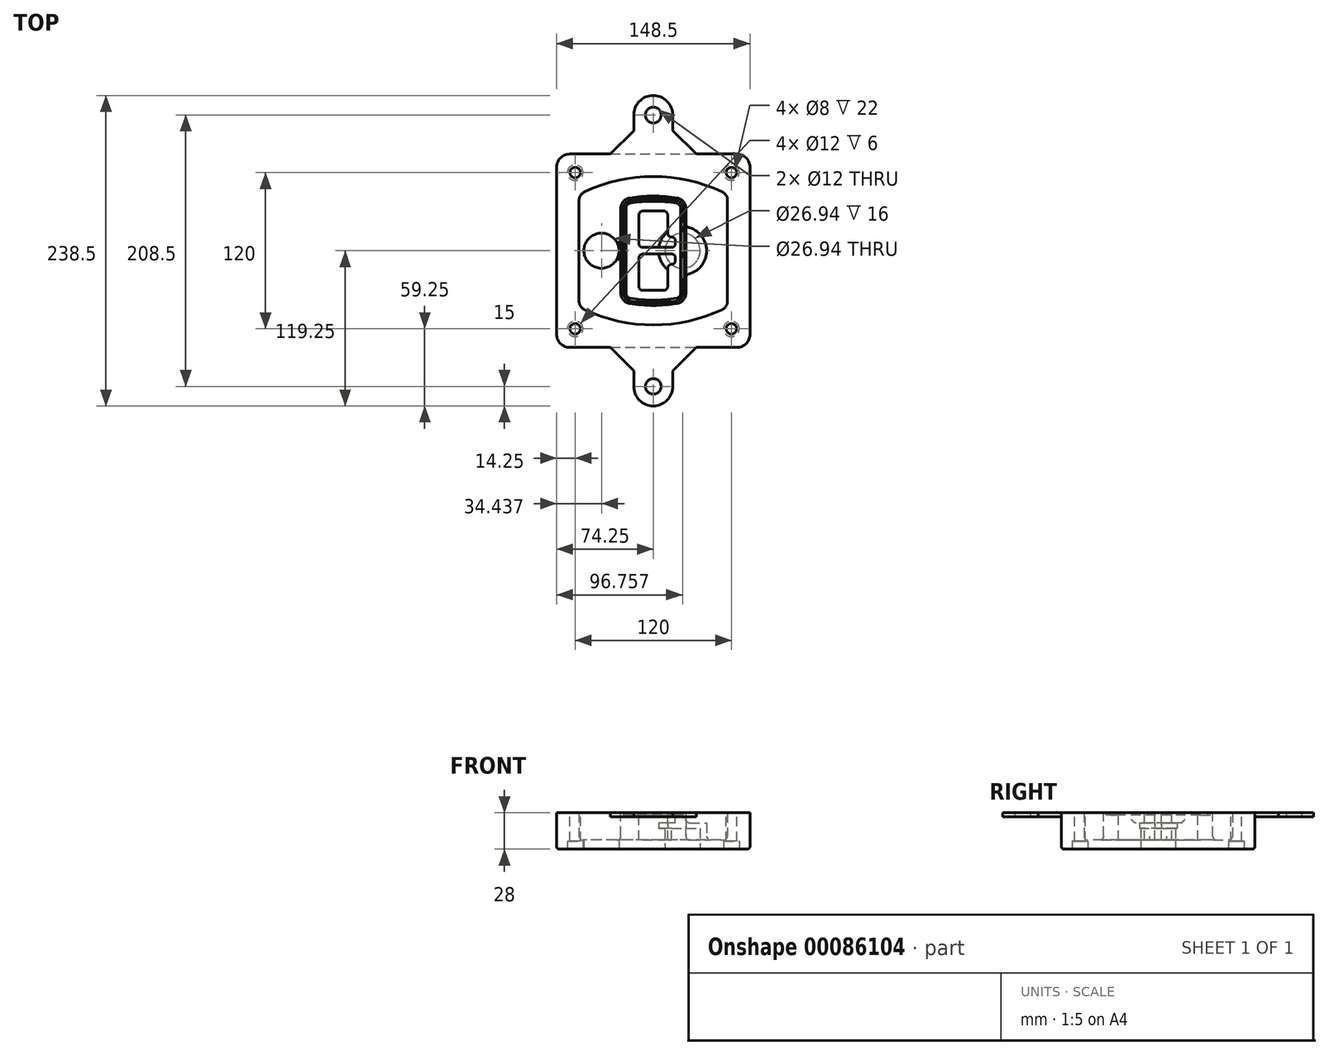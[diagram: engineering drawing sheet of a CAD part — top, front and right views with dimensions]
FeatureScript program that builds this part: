
annotation { "Feature Type Name" : "Feature", "Feature Type Description" : "" }
export const myFeature = defineFeature(function(context is Context, id is Id, definition is map)
    precondition{}
    {
        {
            var Q0;
            Q0=qCreatedBy(makeId("Top.planeOp"),FACE);
            var sketch = newSketch(context, id + "F0", { "sketchPlane" : qUnion([Q0])});
            skPoint(sketch, "E0.rect.middle", {"position": v(0, 0) * mm});
            skLineSegment(sketch, "E1.bottom", {"start": v(-64.25, -74.25) * mm, "end": v(64.25, -74.25) * mm});
            skLineSegment(sketch, "E1.top", {"start": v(-64.25, 74.25) * mm, "end": v(64.25, 74.25) * mm});
            skLineSegment(sketch, "E1.left", {"start": v(-74.25, -64.25) * mm, "end": v(-74.25, 64.25) * mm});
            skLineSegment(sketch, "E1.right", {"start": v(74.25, -64.25) * mm, "end": v(74.25, 64.25) * mm});
            skLineSegment(sketch, "E2", {"start": v(-74.25, 74.25) * mm, "end": v(74.25, -74.25) * mm, "construction": true});
            skLineSegment(sketch, "E3", {"start": v(74.25, 74.25) * mm, "end": v(-74.25, -74.25) * mm, "construction": true});
            skCircle(sketch, "E4", {"center": v(-60, 60) * mm, "radius": 4 * mm});
            skCircle(sketch, "E5", {"center": v(60, 60) * mm, "radius": 4 * mm});
            skCircle(sketch, "E6", {"center": v(60, -60) * mm, "radius": 4 * mm});
            skCircle(sketch, "E7", {"center": v(-60, -60) * mm, "radius": 4 * mm});
            skLineSegment(sketch, "E8", {"start": v(-60, 60) * mm, "end": v(60, 60) * mm, "construction": true});
            skLineSegment(sketch, "E9", {"start": v(60, 60) * mm, "end": v(60, -60) * mm, "construction": true});
            skLineSegment(sketch, "E10", {"start": v(60, -60) * mm, "end": v(-60, -60) * mm, "construction": true});
            skLineSegment(sketch, "E11", {"start": v(-60, -60) * mm, "end": v(-60, 60) * mm, "construction": true});
            skLineSegment(sketch, "E12", {"start": v(-60, 38.83) * mm, "end": v(-60, -38.83) * mm});
            skLineSegment(sketch, "E13", {"start": v(60, 38.83) * mm, "end": v(60, -38.83) * mm});
            skArc(sketch, "E14", {"start": v(54.26, 47.88) * mm, "mid": v(0, 60) * mm, "end": v(-54.26, 47.88) * mm});
            skArc(sketch, "E15", {"start": v(-54.26, -47.88) * mm, "mid": v(0, -60) * mm, "end": v(54.26, -47.88) * mm});
            skLineSegment(sketch, "E16", {"start": v(-60, 0) * mm, "end": v(60, 0) * mm, "construction": true});
            skPoint(sketch, "E17.visualSharp", {"position": v(-60, -45) * mm});
            skArc(sketch, "E17.filletArc", {"start": v(-60, -38.83) * mm, "mid": v(-58.44, -44.2) * mm, "end": v(-54.26, -47.88) * mm});
            skPoint(sketch, "E18.visualSharp", {"position": v(-60, 45) * mm});
            skArc(sketch, "E18.filletArc", {"start": v(-54.26, 47.88) * mm, "mid": v(-58.44, 44.2) * mm, "end": v(-60, 38.83) * mm});
            skPoint(sketch, "E19.visualSharp", {"position": v(60, 45) * mm});
            skArc(sketch, "E19.filletArc", {"start": v(60, 38.83) * mm, "mid": v(58.44, 44.2) * mm, "end": v(54.26, 47.88) * mm});
            skPoint(sketch, "E20.visualSharp", {"position": v(60, -45) * mm});
            skArc(sketch, "E20.filletArc", {"start": v(54.26, -47.88) * mm, "mid": v(58.44, -44.2) * mm, "end": v(60, -38.83) * mm});
            skPoint(sketch, "E21.visualSharp", {"position": v(-74.25, 74.25) * mm});
            skArc(sketch, "E21.filletArc", {"start": v(-64.25, 74.25) * mm, "mid": v(-71.32, 71.32) * mm, "end": v(-74.25, 64.25) * mm});
            skPoint(sketch, "E22.visualSharp", {"position": v(74.25, 74.25) * mm});
            skArc(sketch, "E22.filletArc", {"start": v(74.25, 64.25) * mm, "mid": v(71.32, 71.32) * mm, "end": v(64.25, 74.25) * mm});
            skPoint(sketch, "E23.visualSharp", {"position": v(74.25, -74.25) * mm});
            skArc(sketch, "E23.filletArc", {"start": v(64.25, -74.25) * mm, "mid": v(71.32, -71.32) * mm, "end": v(74.25, -64.25) * mm});
            skPoint(sketch, "E24.visualSharp", {"position": v(-74.25, -74.25) * mm});
            skArc(sketch, "E24.filletArc", {"start": v(-74.25, -64.25) * mm, "mid": v(-71.32, -71.32) * mm, "end": v(-64.25, -74.25) * mm});
            skArc(sketch, "E25.0", {"start": v(57, 38.83) * mm, "mid": v(55.9, 42.58) * mm, "end": v(52.98, 45.17) * mm});
            skLineSegment(sketch, "E25.1", {"start": v(57, 38.83) * mm, "end": v(57, -38.83) * mm});
            skArc(sketch, "E25.2", {"start": v(52.98, -45.17) * mm, "mid": v(55.9, -42.58) * mm, "end": v(57, -38.83) * mm});
            skArc(sketch, "E25.3", {"start": v(-52.98, -45.17) * mm, "mid": v(0, -57) * mm, "end": v(52.98, -45.17) * mm});
            skArc(sketch, "E25.4", {"start": v(-57, -38.83) * mm, "mid": v(-55.9, -42.58) * mm, "end": v(-52.98, -45.17) * mm});
            skArc(sketch, "E25.5", {"start": v(52.98, 45.17) * mm, "mid": v(0, 57) * mm, "end": v(-52.98, 45.17) * mm});
            skLineSegment(sketch, "E25.6", {"start": v(-57, 38.83) * mm, "end": v(-57, -38.83) * mm});
            skArc(sketch, "E25.7", {"start": v(-52.98, 45.17) * mm, "mid": v(-55.9, 42.58) * mm, "end": v(-57, 38.83) * mm});
            skArc(sketch, "E26.0", {"start": v(-55.96, 51.5) * mm, "mid": v(-61.82, 46.33) * mm, "end": v(-64, 38.83) * mm});
            skArc(sketch, "E26.1", {"start": v(55.96, 51.5) * mm, "mid": v(0, 64) * mm, "end": v(-55.96, 51.5) * mm});
            skArc(sketch, "E26.2", {"start": v(64, 38.83) * mm, "mid": v(61.82, 46.33) * mm, "end": v(55.96, 51.5) * mm});
            skLineSegment(sketch, "E26.3", {"start": v(64, 38.83) * mm, "end": v(64, -38.83) * mm});
            skArc(sketch, "E26.4", {"start": v(55.96, -51.5) * mm, "mid": v(61.82, -46.33) * mm, "end": v(64, -38.83) * mm});
            skLineSegment(sketch, "E26.5", {"start": v(-64, 38.83) * mm, "end": v(-64, -38.83) * mm});
            skArc(sketch, "E26.6", {"start": v(-55.96, -51.5) * mm, "mid": v(0, -64) * mm, "end": v(55.96, -51.5) * mm});
            skArc(sketch, "E26.7", {"start": v(-64, -38.83) * mm, "mid": v(-61.82, -46.33) * mm, "end": v(-55.96, -51.5) * mm});
            skSolve(sketch);
        }
        {
            var Q0;
            Q0=makeQuery(id+"F0.imprint","IMPRINT",FACE,{"disambiguationData":[TD([[makeQuery(id+"F0.imprint","IMPRINT",EDGE,{"derivedFrom":sQuery(id+"F0.wireOp",EDGE,"E1.bottom")}),1.0]])]});
            var Q1;
            Q1=makeQuery(id+"F0.imprint","IMPRINT",FACE,{"disambiguationData":[TD([[makeQuery(id+"F0.imprint","IMPRINT",EDGE,{"derivedFrom":sQuery(id+"F0.wireOp",EDGE,"E12")}),1.0]])]});
            var Q2;
            Q2=makeQuery(id+"F0.imprint","IMPRINT",FACE,{"disambiguationData":[TD([[makeQuery(id+"F0.imprint","IMPRINT",EDGE,{"derivedFrom":sQuery(id+"F0.wireOp",EDGE,"E25.0")}),1.0]])]});
            var Q3;
            Q3=makeQuery(id+"F0.imprint","IMPRINT",FACE,{"disambiguationData":[TD([[makeQuery(id+"F0.imprint","IMPRINT",EDGE,{"derivedFrom":sQuery(id+"F0.wireOp",EDGE,"E12")}),-1.0]])]});
            extrude(context, id + "F1", {"entities" : qUnion([Q0, Q1, Q2, Q3]), "oppositeDirection" : true, "depth" : 25 * mm});
        }
        {
            var Q0;
            Q0=makeQuery(id+"F0.imprint","IMPRINT",FACE,{"disambiguationData":[TD([[makeQuery(id+"F0.imprint","IMPRINT",EDGE,{"derivedFrom":sQuery(id+"F0.wireOp",EDGE,"E12")}),1.0]])]});
            extrude(context, id + "F2", {"entities" : qUnion([Q0]), "operationType" : NewBodyOperationType.ADD, "depth" : 3 * mm});
        }
        {
            var Q0;
            Q0=makeQuery(id+"F0.imprint","IMPRINT",FACE,{"disambiguationData":[TD([[makeQuery(id+"F0.imprint","IMPRINT",EDGE,{"derivedFrom":sQuery(id+"F0.wireOp",EDGE,"E25.0")}),1.0]])]});
            extrude(context, id + "F3", {"entities" : qUnion([Q0]), "operationType" : NewBodyOperationType.REMOVE, "oppositeDirection" : true, "depth" : 18 * mm});
        }
        {
            var Q0;
            Q0=makeQuery(id+"F2.opExtrude","CAP_FACE",FACE,{"disambiguationData":[OSD([sQuery(id+"F0.wireOp",EDGE,"E12"),sQuery(id+"F0.wireOp",EDGE,"E13"),sQuery(id+"F0.wireOp",EDGE,"E14"),sQuery(id+"F0.wireOp",EDGE,"E15"),sQuery(id+"F0.wireOp",EDGE,"E17.filletArc"),sQuery(id+"F0.wireOp",EDGE,"E18.filletArc"),sQuery(id+"F0.wireOp",EDGE,"E19.filletArc"),sQuery(id+"F0.wireOp",EDGE,"E20.filletArc"),sQuery(id+"F0.wireOp",EDGE,"E25.0"),sQuery(id+"F0.wireOp",EDGE,"E25.1"),sQuery(id+"F0.wireOp",EDGE,"E25.2"),sQuery(id+"F0.wireOp",EDGE,"E25.3"),sQuery(id+"F0.wireOp",EDGE,"E25.4"),sQuery(id+"F0.wireOp",EDGE,"E25.5"),sQuery(id+"F0.wireOp",EDGE,"E25.6"),sQuery(id+"F0.wireOp",EDGE,"E25.7")])],"isStart":false});
            var sketch = newSketch(context, id + "F4", { "sketchPlane" : qUnion([Q0])});
            skArc(sketch, "E27.0", {"start": v(-18.34, -40.45) * mm, "mid": v(0, -42) * mm, "end": v(18.34, -40.45) * mm});
            skArc(sketch, "E28.0", {"start": v(18.34, 40.45) * mm, "mid": v(0, 42) * mm, "end": v(-18.34, 40.45) * mm});
            skLineSegment(sketch, "E29", {"start": v(-25, 32.57) * mm, "end": v(-25, -32.57) * mm});
            skLineSegment(sketch, "E30", {"start": v(25, 32.57) * mm, "end": v(25, -32.57) * mm});
            skLineSegment(sketch, "E31", {"start": v(-25, 39.1) * mm, "end": v(25, 39.1) * mm, "construction": true});
            skLineSegment(sketch, "E32", {"start": v(-25, -39.1) * mm, "end": v(25, -39.1) * mm, "construction": true});
            skPoint(sketch, "E33.visualSharp", {"position": v(-25, 39.1) * mm});
            skArc(sketch, "E33.filletArc", {"start": v(-18.34, 40.45) * mm, "mid": v(-23.11, 37.73) * mm, "end": v(-25, 32.57) * mm});
            skPoint(sketch, "E34.visualSharp", {"position": v(25, 39.1) * mm});
            skArc(sketch, "E34.filletArc", {"start": v(25, 32.57) * mm, "mid": v(23.11, 37.73) * mm, "end": v(18.34, 40.45) * mm});
            skPoint(sketch, "E35.visualSharp", {"position": v(25, -39.1) * mm});
            skArc(sketch, "E35.filletArc", {"start": v(18.34, -40.45) * mm, "mid": v(23.11, -37.73) * mm, "end": v(25, -32.57) * mm});
            skPoint(sketch, "E36.visualSharp", {"position": v(-25, -39.1) * mm});
            skArc(sketch, "E36.filletArc", {"start": v(-25, -32.57) * mm, "mid": v(-23.11, -37.73) * mm, "end": v(-18.34, -40.45) * mm});
            skArc(sketch, "E37.0", {"start": v(52.98, 45.17) * mm, "mid": v(0, 57) * mm, "end": v(-52.98, 45.17) * mm});
            skArc(sketch, "E37.1", {"start": v(-52.98, 45.17) * mm, "mid": v(-55.9, 42.58) * mm, "end": v(-57, 38.83) * mm});
            skLineSegment(sketch, "E37.2", {"start": v(-57, 38.83) * mm, "end": v(-57, -38.83) * mm});
            skArc(sketch, "E37.3", {"start": v(-57, -38.83) * mm, "mid": v(-55.9, -42.58) * mm, "end": v(-52.98, -45.17) * mm});
            skArc(sketch, "E37.4", {"start": v(-52.98, -45.17) * mm, "mid": v(0, -57) * mm, "end": v(52.98, -45.17) * mm});
            skArc(sketch, "E37.5", {"start": v(52.98, -45.17) * mm, "mid": v(55.9, -42.58) * mm, "end": v(57, -38.83) * mm});
            skLineSegment(sketch, "E37.6", {"start": v(57, 38.83) * mm, "end": v(57, -38.83) * mm});
            skArc(sketch, "E37.7", {"start": v(57, 38.83) * mm, "mid": v(55.9, 42.58) * mm, "end": v(52.98, 45.17) * mm});
            skLineSegment(sketch, "E38.0", {"start": v(23, 32.57) * mm, "end": v(23, -32.57) * mm});
            skArc(sketch, "E38.1", {"start": v(18, -38.48) * mm, "mid": v(21.58, -36.44) * mm, "end": v(23, -32.57) * mm});
            skArc(sketch, "E38.2", {"start": v(-18, -38.48) * mm, "mid": v(0, -40) * mm, "end": v(18, -38.48) * mm});
            skArc(sketch, "E38.3", {"start": v(-23, -32.57) * mm, "mid": v(-21.58, -36.44) * mm, "end": v(-18, -38.48) * mm});
            skLineSegment(sketch, "E38.4", {"start": v(-23, 32.57) * mm, "end": v(-23, -32.57) * mm});
            skArc(sketch, "E38.5", {"start": v(23, 32.57) * mm, "mid": v(21.58, 36.44) * mm, "end": v(18, 38.48) * mm});
            skArc(sketch, "E38.6", {"start": v(-18, 38.48) * mm, "mid": v(-21.58, 36.44) * mm, "end": v(-23, 32.57) * mm});
            skArc(sketch, "E38.7", {"start": v(18, 38.48) * mm, "mid": v(0, 40) * mm, "end": v(-18, 38.48) * mm});
            skArc(sketch, "E39.0", {"start": v(21, 32.57) * mm, "mid": v(20.06, 35.15) * mm, "end": v(17.67, 36.5) * mm});
            skLineSegment(sketch, "E39.1", {"start": v(21, 32.57) * mm, "end": v(21, -32.57) * mm});
            skArc(sketch, "E39.2", {"start": v(17.67, -36.5) * mm, "mid": v(20.06, -35.15) * mm, "end": v(21, -32.57) * mm});
            skArc(sketch, "E39.3", {"start": v(-17.67, -36.5) * mm, "mid": v(0, -38) * mm, "end": v(17.67, -36.5) * mm});
            skArc(sketch, "E39.4", {"start": v(-21, -32.57) * mm, "mid": v(-20.06, -35.15) * mm, "end": v(-17.67, -36.5) * mm});
            skArc(sketch, "E39.5", {"start": v(17.67, 36.5) * mm, "mid": v(0, 38) * mm, "end": v(-17.67, 36.5) * mm});
            skLineSegment(sketch, "E39.6", {"start": v(-21, 32.57) * mm, "end": v(-21, -32.57) * mm});
            skArc(sketch, "E39.7", {"start": v(-17.67, 36.5) * mm, "mid": v(-20.06, 35.15) * mm, "end": v(-21, 32.57) * mm});
            skLineSegment(sketch, "E40", {"start": v(-25, 0) * mm, "end": v(25, 0) * mm, "construction": true});
            skLineSegment(sketch, "E41", {"start": v(-11, 5.5) * mm, "end": v(-11, 27.5) * mm});
            skLineSegment(sketch, "E42", {"start": v(-8, 30.5) * mm, "end": v(8, 30.5) * mm});
            skLineSegment(sketch, "E43", {"start": v(11, 27.5) * mm, "end": v(11, 13.5) * mm});
            skLineSegment(sketch, "E44", {"start": v(14, 10.5) * mm, "end": v(14, 10.5) * mm});
            skLineSegment(sketch, "E45", {"start": v(17, 7.5) * mm, "end": v(17, 5.5) * mm});
            skLineSegment(sketch, "E46", {"start": v(14, 2.5) * mm, "end": v(-8, 2.5) * mm});
            skPoint(sketch, "E47.visualSharp", {"position": v(-11, 30.5) * mm});
            skArc(sketch, "E47.filletArc", {"start": v(-8, 30.5) * mm, "mid": v(-10.12, 29.62) * mm, "end": v(-11, 27.5) * mm});
            skPoint(sketch, "E48.visualSharp", {"position": v(11, 30.5) * mm});
            skArc(sketch, "E48.filletArc", {"start": v(11, 27.5) * mm, "mid": v(10.12, 29.62) * mm, "end": v(8, 30.5) * mm});
            skPoint(sketch, "E49.visualSharp", {"position": v(11, 10.5) * mm});
            skArc(sketch, "E49.filletArc", {"start": v(11, 13.5) * mm, "mid": v(11.88, 11.38) * mm, "end": v(14, 10.5) * mm});
            skPoint(sketch, "E50.visualSharp", {"position": v(17, 10.5) * mm});
            skArc(sketch, "E50.filletArc", {"start": v(17, 7.5) * mm, "mid": v(16.12, 9.62) * mm, "end": v(14, 10.5) * mm});
            skPoint(sketch, "E51.visualSharp", {"position": v(17, 2.5) * mm});
            skArc(sketch, "E51.filletArc", {"start": v(14, 2.5) * mm, "mid": v(16.12, 3.38) * mm, "end": v(17, 5.5) * mm});
            skPoint(sketch, "E52.visualSharp", {"position": v(-11, 2.5) * mm});
            skArc(sketch, "E52.filletArc", {"start": v(-11, 5.5) * mm, "mid": v(-10.12, 3.38) * mm, "end": v(-8, 2.5) * mm});
            skLineSegment(sketch, "E53.0.MirrorCS", {"start": v(14, -2.5) * mm, "end": v(-8, -2.5) * mm});
            skArc(sketch, "E54.0.MirrorCS", {"start": v(-11, -5.5) * mm, "mid": v(-10.12, -3.38) * mm, "end": v(-8, -2.5) * mm});
            skLineSegment(sketch, "E55.0.MirrorCS", {"start": v(-11, -5.5) * mm, "end": v(-11, -27.5) * mm});
            skArc(sketch, "E56.0.MirrorCS", {"start": v(-8, -30.5) * mm, "mid": v(-10.12, -29.62) * mm, "end": v(-11, -27.5) * mm});
            skLineSegment(sketch, "E57.0.MirrorCS", {"start": v(-8, -30.5) * mm, "end": v(8, -30.5) * mm});
            skArc(sketch, "E58.0.MirrorCS", {"start": v(11, -27.5) * mm, "mid": v(10.12, -29.62) * mm, "end": v(8, -30.5) * mm});
            skLineSegment(sketch, "E59.0.MirrorCS", {"start": v(11, -27.5) * mm, "end": v(11, -13.5) * mm});
            skArc(sketch, "E60.0.MirrorCS", {"start": v(11, -13.5) * mm, "mid": v(11.88, -11.38) * mm, "end": v(14, -10.5) * mm});
            skArc(sketch, "E61.0.MirrorCS", {"start": v(17, -7.5) * mm, "mid": v(16.12, -9.62) * mm, "end": v(14, -10.5) * mm});
            skLineSegment(sketch, "E62.0.MirrorCS", {"start": v(17, -7.5) * mm, "end": v(17, -5.5) * mm});
            skArc(sketch, "E63.0.MirrorCS", {"start": v(14, -2.5) * mm, "mid": v(16.12, -3.38) * mm, "end": v(17, -5.5) * mm});
            skSolve(sketch);
        }
        {
            var Q0;
            Q0=makeQuery(id+"F4.imprint","IMPRINT",FACE,{"disambiguationData":[TD([[makeQuery(id+"F4.imprint","IMPRINT",EDGE,{"derivedFrom":sQuery(id+"F4.wireOp",EDGE,"E27.0")}),1.0]])]});
            var Q1;
            Q1=makeQuery(id+"F4.imprint","IMPRINT",FACE,{"disambiguationData":[TD([[makeQuery(id+"F4.imprint","IMPRINT",EDGE,{"derivedFrom":sQuery(id+"F4.wireOp",EDGE,"E38.0")}),-1.0]])]});
            var Q2;
            Q2=makeQuery(id+"F4.imprint","IMPRINT",FACE,{"disambiguationData":[TD([[makeQuery(id+"F4.imprint","IMPRINT",EDGE,{"derivedFrom":sQuery(id+"F4.wireOp",EDGE,"E39.0")}),1.0]])]});
            extrude(context, id + "F5", {"entities" : qUnion([Q0, Q1, Q2]), "operationType" : NewBodyOperationType.ADD, "endBound" : BoundingType.UP_TO_NEXT, "oppositeDirection" : true, "depth" : 25 * mm});
        }
        {
            var Q0;
            Q0=makeQuery(id+"F4.imprint","IMPRINT",FACE,{"disambiguationData":[TD([[makeQuery(id+"F4.imprint","IMPRINT",EDGE,{"derivedFrom":sQuery(id+"F4.wireOp",EDGE,"E38.0")}),-1.0]])]});
            extrude(context, id + "F6", {"entities" : qUnion([Q0]), "operationType" : NewBodyOperationType.REMOVE, "oppositeDirection" : true, "depth" : 2 * mm});
        }
        {
            var Q0;
            Q0=makeQuery(id+"F1.opExtrude","CAP_FACE",FACE,{"disambiguationData":[OSD([sQuery(id+"F0.wireOp",EDGE,"E1.bottom"),sQuery(id+"F0.wireOp",EDGE,"E1.top"),sQuery(id+"F0.wireOp",EDGE,"E1.left"),sQuery(id+"F0.wireOp",EDGE,"E1.right"),sQuery(id+"F0.wireOp",EDGE,"E4"),sQuery(id+"F0.wireOp",EDGE,"E5"),sQuery(id+"F0.wireOp",EDGE,"E6"),sQuery(id+"F0.wireOp",EDGE,"E7"),sQuery(id+"F0.wireOp",EDGE,"E21.filletArc"),sQuery(id+"F0.wireOp",EDGE,"E22.filletArc"),sQuery(id+"F0.wireOp",EDGE,"E23.filletArc"),sQuery(id+"F0.wireOp",EDGE,"E24.filletArc")])],"isStart":false});
            var sketch = newSketch(context, id + "F7", { "sketchPlane" : qUnion([Q0])});
            skCircle(sketch, "E64", {"center": v(22.5, 0) * mm, "radius": 13.47 * mm});
            skCircle(sketch, "E65", {"center": v(-39.81, 0) * mm, "radius": 13.47 * mm});
            skLineSegment(sketch, "E66", {"start": v(74.25, 0) * mm, "end": v(-74.25, 0) * mm});
            skCircle(sketch, "E67", {"center": v(22.5, 0) * mm, "radius": 18.47 * mm});
            skCircle(sketch, "E68", {"center": v(60, -60) * mm, "radius": 6 * mm});
            skCircle(sketch, "E69", {"center": v(-60, -60) * mm, "radius": 6 * mm});
            skCircle(sketch, "E70", {"center": v(-60, 60) * mm, "radius": 6 * mm});
            skCircle(sketch, "E71", {"center": v(60, 60) * mm, "radius": 6 * mm});
            skSolve(sketch);
        }
        {
            var Q0;
            {var subQ1=sQuery(id+"F7.wireOp",EDGE,"E66");var subQ4=sQuery(id+"F7.wireOp",EDGE,"E64");var subQ6=makeQuery(id+"F7.imprint","INTERSECT",VERTEX,{"disambiguationData":[OD(0.0)],"derivedFrom":[subQ4,subQ1]});Q0=makeQuery(id+"F7.imprint","IMPRINT",FACE,{"disambiguationData":[TD([[makeQuery(id+"F7.imprint","IMPRINT",EDGE,{"disambiguationData":[TD([[subQ6,-1.0]])],"derivedFrom":subQ4}),-1.0]])]});}
            var Q1;
            {var subQ0=sQuery(id+"F7.wireOp",EDGE,"E66");var subQ1=sQuery(id+"F7.wireOp",EDGE,"E64");var subQ3=makeQuery(id+"F7.imprint","INTERSECT",VERTEX,{"disambiguationData":[OD(0.0)],"derivedFrom":[subQ1,subQ0]});Q1=makeQuery(id+"F7.imprint","IMPRINT",FACE,{"disambiguationData":[TD([[makeQuery(id+"F7.imprint","IMPRINT",EDGE,{"disambiguationData":[TD([[subQ3,-1.0]])],"derivedFrom":subQ1}),1.0]])]});}
            var Q2;
            {var subQ0=sQuery(id+"F7.wireOp",EDGE,"E66");var subQ1=sQuery(id+"F7.wireOp",EDGE,"E64");var subQ3=makeQuery(id+"F7.imprint","INTERSECT",VERTEX,{"disambiguationData":[OD(0.0)],"derivedFrom":[subQ1,subQ0]});Q2=makeQuery(id+"F7.imprint","IMPRINT",FACE,{"disambiguationData":[TD([[makeQuery(id+"F7.imprint","IMPRINT",EDGE,{"disambiguationData":[TD([[subQ3,1.0]])],"derivedFrom":subQ1}),1.0]])]});}
            var Q3;
            {var subQ1=sQuery(id+"F7.wireOp",EDGE,"E66");var subQ4=sQuery(id+"F7.wireOp",EDGE,"E64");var subQ6=makeQuery(id+"F7.imprint","INTERSECT",VERTEX,{"disambiguationData":[OD(0.0)],"derivedFrom":[subQ4,subQ1]});Q3=makeQuery(id+"F7.imprint","IMPRINT",FACE,{"disambiguationData":[TD([[makeQuery(id+"F7.imprint","IMPRINT",EDGE,{"disambiguationData":[TD([[subQ6,1.0]])],"derivedFrom":subQ4}),-1.0]])]});}
            extrude(context, id + "F8", {"entities" : qUnion([Q0, Q1, Q2, Q3]), "operationType" : NewBodyOperationType.ADD, "oppositeDirection" : true, "depth" : 20 * mm});
        }
        {
            var Q0;
            {var subQ0=sQuery(id+"F7.wireOp",EDGE,"E66");var subQ1=sQuery(id+"F7.wireOp",EDGE,"E64");var subQ3=makeQuery(id+"F7.imprint","INTERSECT",VERTEX,{"disambiguationData":[OD(0.0)],"derivedFrom":[subQ1,subQ0]});Q0=makeQuery(id+"F7.imprint","IMPRINT",FACE,{"disambiguationData":[TD([[makeQuery(id+"F7.imprint","IMPRINT",EDGE,{"disambiguationData":[TD([[subQ3,-1.0]])],"derivedFrom":subQ1}),1.0]])]});}
            var Q1;
            {var subQ0=sQuery(id+"F7.wireOp",EDGE,"E66");var subQ1=sQuery(id+"F7.wireOp",EDGE,"E64");var subQ3=makeQuery(id+"F7.imprint","INTERSECT",VERTEX,{"disambiguationData":[OD(0.0)],"derivedFrom":[subQ1,subQ0]});Q1=makeQuery(id+"F7.imprint","IMPRINT",FACE,{"disambiguationData":[TD([[makeQuery(id+"F7.imprint","IMPRINT",EDGE,{"disambiguationData":[TD([[subQ3,1.0]])],"derivedFrom":subQ1}),1.0]])]});}
            extrude(context, id + "F9", {"entities" : qUnion([Q0, Q1]), "operationType" : NewBodyOperationType.REMOVE, "oppositeDirection" : true, "depth" : 16 * mm});
        }
        {
            var Q0;
            {var subQ0=sQuery(id+"F7.wireOp",EDGE,"E66");var subQ1=sQuery(id+"F7.wireOp",EDGE,"E65");var subQ3=makeQuery(id+"F7.imprint","INTERSECT",VERTEX,{"disambiguationData":[OD(0.0)],"derivedFrom":[subQ1,subQ0]});Q0=makeQuery(id+"F7.imprint","IMPRINT",FACE,{"disambiguationData":[TD([[makeQuery(id+"F7.imprint","IMPRINT",EDGE,{"disambiguationData":[TD([[subQ3,-1.0]])],"derivedFrom":subQ1}),1.0]])]});}
            var Q1;
            {var subQ0=sQuery(id+"F7.wireOp",EDGE,"E66");var subQ1=sQuery(id+"F7.wireOp",EDGE,"E65");var subQ3=makeQuery(id+"F7.imprint","INTERSECT",VERTEX,{"disambiguationData":[OD(0.0)],"derivedFrom":[subQ1,subQ0]});Q1=makeQuery(id+"F7.imprint","IMPRINT",FACE,{"disambiguationData":[TD([[makeQuery(id+"F7.imprint","IMPRINT",EDGE,{"disambiguationData":[TD([[subQ3,1.0]])],"derivedFrom":subQ1}),1.0]])]});}
            extrude(context, id + "F10", {"entities" : qUnion([Q0, Q1]), "operationType" : NewBodyOperationType.REMOVE, "oppositeDirection" : true, "depth" : 25 * mm});
        }
        {
            var Q0;
            Q0=makeQuery(id+"F7.imprint","IMPRINT",FACE,{"disambiguationData":[TD([[makeQuery(id+"F7.imprint","IMPRINT",EDGE,{"derivedFrom":sQuery(id+"F7.wireOp",EDGE,"E68")}),1.0]])]});
            var Q1;
            Q1=makeQuery(id+"F7.imprint","IMPRINT",FACE,{"disambiguationData":[TD([[makeQuery(id+"F7.imprint","IMPRINT",EDGE,{"derivedFrom":makeQuery(id+"F1.opExtrude","CAP_EDGE",EDGE,{"disambiguationData":[OSD([sQuery(id+"F0.wireOp",EDGE,"E5")])],"isStart":false})}),-1.0]])]});
            var Q2;
            Q2=makeQuery(id+"F7.imprint","IMPRINT",FACE,{"disambiguationData":[TD([[makeQuery(id+"F7.imprint","IMPRINT",EDGE,{"derivedFrom":sQuery(id+"F7.wireOp",EDGE,"E69")}),1.0]])]});
            var Q3;
            Q3=makeQuery(id+"F7.imprint","IMPRINT",FACE,{"disambiguationData":[TD([[makeQuery(id+"F7.imprint","IMPRINT",EDGE,{"derivedFrom":makeQuery(id+"F1.opExtrude","CAP_EDGE",EDGE,{"disambiguationData":[OSD([sQuery(id+"F0.wireOp",EDGE,"E4")])],"isStart":false})}),-1.0]])]});
            var Q4;
            Q4=makeQuery(id+"F7.imprint","IMPRINT",FACE,{"disambiguationData":[TD([[makeQuery(id+"F7.imprint","IMPRINT",EDGE,{"derivedFrom":sQuery(id+"F7.wireOp",EDGE,"E70")}),1.0]])]});
            var Q5;
            Q5=makeQuery(id+"F7.imprint","IMPRINT",FACE,{"disambiguationData":[TD([[makeQuery(id+"F7.imprint","IMPRINT",EDGE,{"derivedFrom":makeQuery(id+"F1.opExtrude","CAP_EDGE",EDGE,{"disambiguationData":[OSD([sQuery(id+"F0.wireOp",EDGE,"E7")])],"isStart":false})}),-1.0]])]});
            var Q6;
            Q6=makeQuery(id+"F7.imprint","IMPRINT",FACE,{"disambiguationData":[TD([[makeQuery(id+"F7.imprint","IMPRINT",EDGE,{"derivedFrom":sQuery(id+"F7.wireOp",EDGE,"E71")}),1.0]])]});
            var Q7;
            Q7=makeQuery(id+"F7.imprint","IMPRINT",FACE,{"disambiguationData":[TD([[makeQuery(id+"F7.imprint","IMPRINT",EDGE,{"derivedFrom":makeQuery(id+"F1.opExtrude","CAP_EDGE",EDGE,{"disambiguationData":[OSD([sQuery(id+"F0.wireOp",EDGE,"E6")])],"isStart":false})}),-1.0]])]});
            extrude(context, id + "F11", {"entities" : qUnion([Q0, Q1, Q2, Q3, Q4, Q5, Q6, Q7]), "operationType" : NewBodyOperationType.REMOVE, "oppositeDirection" : true, "depth" : 6 * mm});
        }
        {
            var Q0;
            Q0=makeQuery(id+"F9.boolean.opBoolean","COPY",FACE,{"derivedFrom":makeQuery(id+"F9.opExtrude","CAP_FACE",FACE,{"disambiguationData":[OSD([sQuery(id+"F7.wireOp",EDGE,"E64")])],"isStart":false})});
            var sketch = newSketch(context, id + "F12", { "sketchPlane" : qUnion([Q0])});
            skArc(sketch, "E72.0", {"start": v(11, 14.45) * mm, "mid": v(6.45, 9.13) * mm, "end": v(4.2, 2.5) * mm});
            skArc(sketch, "E72.1", {"start": v(4.2, -2.5) * mm, "mid": v(6.45, -9.13) * mm, "end": v(11, -14.45) * mm});
            skLineSegment(sketch, "E73", {"start": v(4.2, -2.5) * mm, "end": v(14, -2.5) * mm});
            skLineSegment(sketch, "E74.0", {"start": v(14, 2.5) * mm, "end": v(4.2, 2.5) * mm});
            skArc(sketch, "E74.1", {"start": v(14, 2.5) * mm, "mid": v(16.12, 3.38) * mm, "end": v(17, 5.5) * mm});
            skLineSegment(sketch, "E74.2", {"start": v(17, 7.5) * mm, "end": v(17, 5.5) * mm});
            skArc(sketch, "E74.3", {"start": v(17, 7.5) * mm, "mid": v(16.12, 9.62) * mm, "end": v(14, 10.5) * mm});
            skArc(sketch, "E74.4", {"start": v(11, 13.5) * mm, "mid": v(11.88, 11.38) * mm, "end": v(14, 10.5) * mm});
            skLineSegment(sketch, "E74.5", {"start": v(11, 14.45) * mm, "end": v(11, 13.5) * mm});
            skLineSegment(sketch, "E74.7", {"start": v(14, -2.5) * mm, "end": v(4.2, -2.5) * mm});
            skArc(sketch, "E74.8", {"start": v(14, -2.5) * mm, "mid": v(16.12, -3.38) * mm, "end": v(17, -5.5) * mm});
            skLineSegment(sketch, "E74.9", {"start": v(17, -7.5) * mm, "end": v(17, -5.5) * mm});
            skArc(sketch, "E74.10", {"start": v(17, -7.5) * mm, "mid": v(16.12, -9.62) * mm, "end": v(14, -10.5) * mm});
            skArc(sketch, "E74.11", {"start": v(11, -13.5) * mm, "mid": v(11.88, -11.38) * mm, "end": v(14, -10.5) * mm});
            skLineSegment(sketch, "E74.12", {"start": v(11, -14.45) * mm, "end": v(11, -13.5) * mm});
            skPoint(sketch, "E75.orphan", {"position": v(11, -27.5) * mm});
            skPoint(sketch, "E76.orphan", {"position": v(-8, -2.5) * mm});
            skPoint(sketch, "E77.orphan", {"position": v(-8, 2.5) * mm});
            skPoint(sketch, "E78.orphan", {"position": v(11, 27.5) * mm});
            skSolve(sketch);
        }
        {
            var Q0;
            {var subQ7=sQuery(id+"F12.wireOp",EDGE,"E72.0");var subQ14=sQuery(id+"F12.wireOp",EDGE,"E72.1");var subQ16=sQuery(id+"F12.wireOp",EDGE,"E74.1");var subQ18=sQuery(id+"F12.wireOp",EDGE,"E74.8");Q0=qUnion([makeQuery(id+"F12.imprint","IMPRINT",FACE,{"disambiguationData":[TD([[makeQuery(id+"F12.imprint","IMPRINT",EDGE,{"derivedFrom":subQ7}),1.0]])]}),makeQuery(id+"F12.imprint","IMPRINT",FACE,{"disambiguationData":[TD([[makeQuery(id+"F12.imprint","IMPRINT",EDGE,{"derivedFrom":subQ14}),1.0]])]}),makeQuery(id+"F12.imprint","IMPRINT",FACE,{"disambiguationData":[TD([[makeQuery(id+"F12.imprint","IMPRINT",EDGE,{"derivedFrom":subQ16}),1.0]])]}),makeQuery(id+"F12.imprint","IMPRINT",FACE,{"disambiguationData":[TD([[makeQuery(id+"F12.imprint","IMPRINT",EDGE,{"derivedFrom":subQ18}),-1.0]])]})]);}
            var Q1;
            Q1=makeQuery(id+"F5.boolean.opBoolean","SPLIT",FACE,{"disambiguationData":[TD([makeQuery(id+"F5.opExtrude","SWEPT_FACE",FACE,{"disambiguationData":[OSD([sQuery(id+"F4.wireOp",EDGE,"E41")])]})])],"derivedFrom":makeQuery(id+"F3.boolean.opBoolean","COPY",FACE,{"derivedFrom":makeQuery(id+"F3.opExtrude","CAP_FACE",FACE,{"disambiguationData":[OSD([sQuery(id+"F0.wireOp",EDGE,"E25.0"),sQuery(id+"F0.wireOp",EDGE,"E25.1"),sQuery(id+"F0.wireOp",EDGE,"E25.2"),sQuery(id+"F0.wireOp",EDGE,"E25.3"),sQuery(id+"F0.wireOp",EDGE,"E25.4"),sQuery(id+"F0.wireOp",EDGE,"E25.5"),sQuery(id+"F0.wireOp",EDGE,"E25.6"),sQuery(id+"F0.wireOp",EDGE,"E25.7")])],"isStart":false})})});
            extrude(context, id + "F13", {"entities" : qUnion([Q0]), "operationType" : NewBodyOperationType.REMOVE, "endBound" : BoundingType.UP_TO_SURFACE, "endBoundEntityFace" : qUnion([Q1]), "depth" : 25 * mm});
        }
        {
            var Q0;
            Q0=makeQuery(id+"F3.boolean.opBoolean","COPY",EDGE,{"derivedFrom":makeQuery(id+"F3.opExtrude","CAP_EDGE",EDGE,{"disambiguationData":[OSD([sQuery(id+"F0.wireOp",EDGE,"E25.6")])],"isStart":false})});
            var Q1;
            Q1=makeQuery(id+"F8.boolean.opBoolean","INTERSECT",EDGE,{"derivedFrom":[makeQuery(id+"F5.opExtrude","SWEPT_FACE",FACE,{"disambiguationData":[OSD([sQuery(id+"F4.wireOp",EDGE,"E30")])]}),makeQuery(id+"F8.opExtrude","CAP_FACE",FACE,{"disambiguationData":[OSD([sQuery(id+"F7.wireOp",EDGE,"E67")])],"isStart":false})]});
            var Q2;
            Q2=makeQuery(id+"F8.boolean.opBoolean","INTERSECT",EDGE,{"disambiguationData":[OD(1.0)],"derivedFrom":[makeQuery(id+"F5.opExtrude","SWEPT_FACE",FACE,{"disambiguationData":[OSD([sQuery(id+"F4.wireOp",EDGE,"E30")])]}),makeQuery(id+"F8.opExtrude","SWEPT_FACE",FACE,{"disambiguationData":[OSD([sQuery(id+"F7.wireOp",EDGE,"E67")])]})]});
            var Q3;
            {var subQ0=sQuery(id+"F4.wireOp",EDGE,"E30");Q3=makeQuery(id+"F8.boolean.opBoolean","SPLIT",EDGE,{"disambiguationData":[TD([makeQuery(id+"F5.opExtrude","SWEPT_FACE",FACE,{"disambiguationData":[OSD([sQuery(id+"F4.wireOp",EDGE,"E35.filletArc")])]})])],"derivedFrom":makeQuery(id+"F5.opExtrude","CAP_EDGE",EDGE,{"disambiguationData":[OSD([subQ0])],"isStart":false})});}
            var Q4;
            {var subQ0=sQuery(id+"F0.wireOp",EDGE,"E25.7");var subQ1=sQuery(id+"F0.wireOp",EDGE,"E25.1");var subQ2=sQuery(id+"F0.wireOp",EDGE,"E25.6");var subQ3=sQuery(id+"F0.wireOp",EDGE,"E25.5");var subQ4=sQuery(id+"F0.wireOp",EDGE,"E25.4");var subQ5=sQuery(id+"F0.wireOp",EDGE,"E25.0");var subQ6=sQuery(id+"F0.wireOp",EDGE,"E25.2");var subQ7=sQuery(id+"F0.wireOp",EDGE,"E25.3");Q4=makeQuery(id+"F8.boolean.opBoolean","INTERSECT",EDGE,{"derivedFrom":[makeQuery(id+"F5.boolean.opBoolean","SPLIT",FACE,{"disambiguationData":[TD([makeQuery(id+"F2.opExtrude","SWEPT_FACE",FACE,{"disambiguationData":[OSD([subQ5])]})])],"derivedFrom":makeQuery(id+"F3.boolean.opBoolean","COPY",FACE,{"derivedFrom":makeQuery(id+"F3.opExtrude","CAP_FACE",FACE,{"disambiguationData":[OSD([subQ5,subQ1,subQ6,subQ7,subQ4,subQ3,subQ2,subQ0])],"isStart":false})})}),makeQuery(id+"F8.opExtrude","SWEPT_FACE",FACE,{"disambiguationData":[OSD([sQuery(id+"F7.wireOp",EDGE,"E67")])]})]});}
            var Q5;
            Q5=makeQuery(id+"F8.boolean.opBoolean","INTERSECT",EDGE,{"disambiguationData":[OD(0.0)],"derivedFrom":[makeQuery(id+"F5.opExtrude","SWEPT_FACE",FACE,{"disambiguationData":[OSD([sQuery(id+"F4.wireOp",EDGE,"E30")])]}),makeQuery(id+"F8.opExtrude","SWEPT_FACE",FACE,{"disambiguationData":[OSD([sQuery(id+"F7.wireOp",EDGE,"E67")])]})]});
            fillet(context, id + "F14", {"entities" : qUnion([Q0, Q1, Q2, Q3, Q4, Q5]), "radius" : 3 * mm, "tangentPropagation" : true, "allowEdgeOverflow" : false});
        }
        {
            var Q0;
            Q0=makeQuery(id+"F1.opExtrude","CAP_EDGE",EDGE,{"disambiguationData":[OSD([sQuery(id+"F0.wireOp",EDGE,"E1.bottom")])],"isStart":false});
            fillet(context, id + "F15", {"entities" : qUnion([Q0]), "radius" : 2 * mm, "tangentPropagation" : true, "allowEdgeOverflow" : false});
        }
        {
            var Q0;
            {var subQ0=sQuery(id+"F0.wireOp",EDGE,"E22.filletArc");var subQ1=sQuery(id+"F0.wireOp",EDGE,"E7");var subQ2=sQuery(id+"F0.wireOp",EDGE,"E6");var subQ3=sQuery(id+"F0.wireOp",EDGE,"E5");var subQ4=sQuery(id+"F0.wireOp",EDGE,"E4");var subQ5=sQuery(id+"F0.wireOp",EDGE,"E1.bottom");var subQ6=sQuery(id+"F0.wireOp",EDGE,"E21.filletArc");var subQ7=sQuery(id+"F0.wireOp",EDGE,"E1.top");var subQ8=sQuery(id+"F0.wireOp",EDGE,"E1.left");var subQ9=sQuery(id+"F0.wireOp",EDGE,"E1.right");var subQ10=sQuery(id+"F0.wireOp",EDGE,"E23.filletArc");var subQ11=sQuery(id+"F0.wireOp",EDGE,"E24.filletArc");Q0=makeQuery(id+"F2.boolean.opBoolean","SPLIT",FACE,{"disambiguationData":[TD([makeQuery(id+"F1.opExtrude","SWEPT_FACE",FACE,{"disambiguationData":[OSD([subQ5])]})])],"derivedFrom":makeQuery(id+"F1.opExtrude","CAP_FACE",FACE,{"disambiguationData":[OSD([subQ5,subQ7,subQ8,subQ9,subQ4,subQ3,subQ2,subQ1,subQ6,subQ0,subQ10,subQ11])],"isStart":true})});}
            var sketch = newSketch(context, id + "F16", { "sketchPlane" : qUnion([Q0])});
            skLineSegment(sketch, "E79", {"start": v(0, 74.25) * mm, "end": v(0, 104.25) * mm, "construction": true});
            skCircle(sketch, "E80", {"center": v(0, 104.25) * mm, "radius": 6 * mm});
            skLineSegment(sketch, "E81", {"start": v(-15.03, 104.25) * mm, "end": v(-15.03, 92.25) * mm});
            skLineSegment(sketch, "E82", {"start": v(14.97, 104.25) * mm, "end": v(14.97, 92.25) * mm});
            skArc(sketch, "E83", {"start": v(14.97, 104.25) * mm, "mid": v(-0.03, 119.25) * mm, "end": v(-15.03, 104.25) * mm});
            skLineSegment(sketch, "E84", {"start": v(14.97, 92.25) * mm, "end": v(32.97, 74.25) * mm});
            skLineSegment(sketch, "E85", {"start": v(-15.03, 92.25) * mm, "end": v(-33.03, 74.25) * mm});
            skLineSegment(sketch, "E86.0", {"start": v(-64.25, 74.25) * mm, "end": v(64.25, 74.25) * mm});
            skLineSegment(sketch, "E87.MirrorCS", {"start": v(14.97, -92.25) * mm, "end": v(32.97, -74.25) * mm});
            skLineSegment(sketch, "E88.MirrorCS", {"start": v(14.97, -104.25) * mm, "end": v(14.97, -92.25) * mm});
            skArc(sketch, "E89.MirrorCS", {"start": v(14.97, -104.25) * mm, "mid": v(-0.03, -119.25) * mm, "end": v(-15.03, -104.25) * mm});
            skLineSegment(sketch, "E90.MirrorCS", {"start": v(-15.03, -104.25) * mm, "end": v(-15.03, -92.25) * mm});
            skLineSegment(sketch, "E91.MirrorCS", {"start": v(-15.03, -92.25) * mm, "end": v(-33.03, -74.25) * mm});
            skCircle(sketch, "E92.MirrorC", {"center": v(0, -104.25) * mm, "radius": 6 * mm});
            skLineSegment(sketch, "E93.0", {"start": v(-64.25, -74.25) * mm, "end": v(64.25, -74.25) * mm});
            skSolve(sketch);
        }
        {
            var Q0;
            Q0=makeQuery(id+"F16.imprint","IMPRINT",FACE,{"disambiguationData":[TD([[makeQuery(id+"F16.imprint","IMPRINT",EDGE,{"derivedFrom":makeQuery(id+"F1.opExtrude","CAP_EDGE",EDGE,{"disambiguationData":[OSD([sQuery(id+"F0.wireOp",EDGE,"E1.left")])],"isStart":true})}),-1.0]])]});
            var Q1;
            Q1=makeQuery(id+"F16.imprint","IMPRINT",FACE,{"disambiguationData":[TD([[makeQuery(id+"F16.imprint","IMPRINT",EDGE,{"derivedFrom":sQuery(id+"F16.wireOp",EDGE,"E80")}),-1.0]])]});
            var Q2;
            {var subQ0=sQuery(id+"F16.wireOp",EDGE,"E87.MirrorCS");Q2=makeQuery(id+"F16.imprint","IMPRINT",FACE,{"disambiguationData":[TD([[makeQuery(id+"F16.imprint","IMPRINT",EDGE,{"derivedFrom":subQ0}),1.0]])]});}
            var Q3;
            Q3=makeQuery(id+"F2.opExtrude","CAP_FACE",FACE,{"disambiguationData":[OSD([sQuery(id+"F0.wireOp",EDGE,"E12"),sQuery(id+"F0.wireOp",EDGE,"E13"),sQuery(id+"F0.wireOp",EDGE,"E14"),sQuery(id+"F0.wireOp",EDGE,"E15"),sQuery(id+"F0.wireOp",EDGE,"E17.filletArc"),sQuery(id+"F0.wireOp",EDGE,"E18.filletArc"),sQuery(id+"F0.wireOp",EDGE,"E19.filletArc"),sQuery(id+"F0.wireOp",EDGE,"E20.filletArc"),sQuery(id+"F0.wireOp",EDGE,"E25.0"),sQuery(id+"F0.wireOp",EDGE,"E25.1"),sQuery(id+"F0.wireOp",EDGE,"E25.2"),sQuery(id+"F0.wireOp",EDGE,"E25.3"),sQuery(id+"F0.wireOp",EDGE,"E25.4"),sQuery(id+"F0.wireOp",EDGE,"E25.5"),sQuery(id+"F0.wireOp",EDGE,"E25.6"),sQuery(id+"F0.wireOp",EDGE,"E25.7")])],"isStart":false});
            extrude(context, id + "F17", {"entities" : qUnion([Q0, Q1, Q2]), "operationType" : NewBodyOperationType.ADD, "endBound" : BoundingType.UP_TO_SURFACE, "endBoundEntityFace" : qUnion([Q3]), "depth" : 25 * mm});
        }
    });
